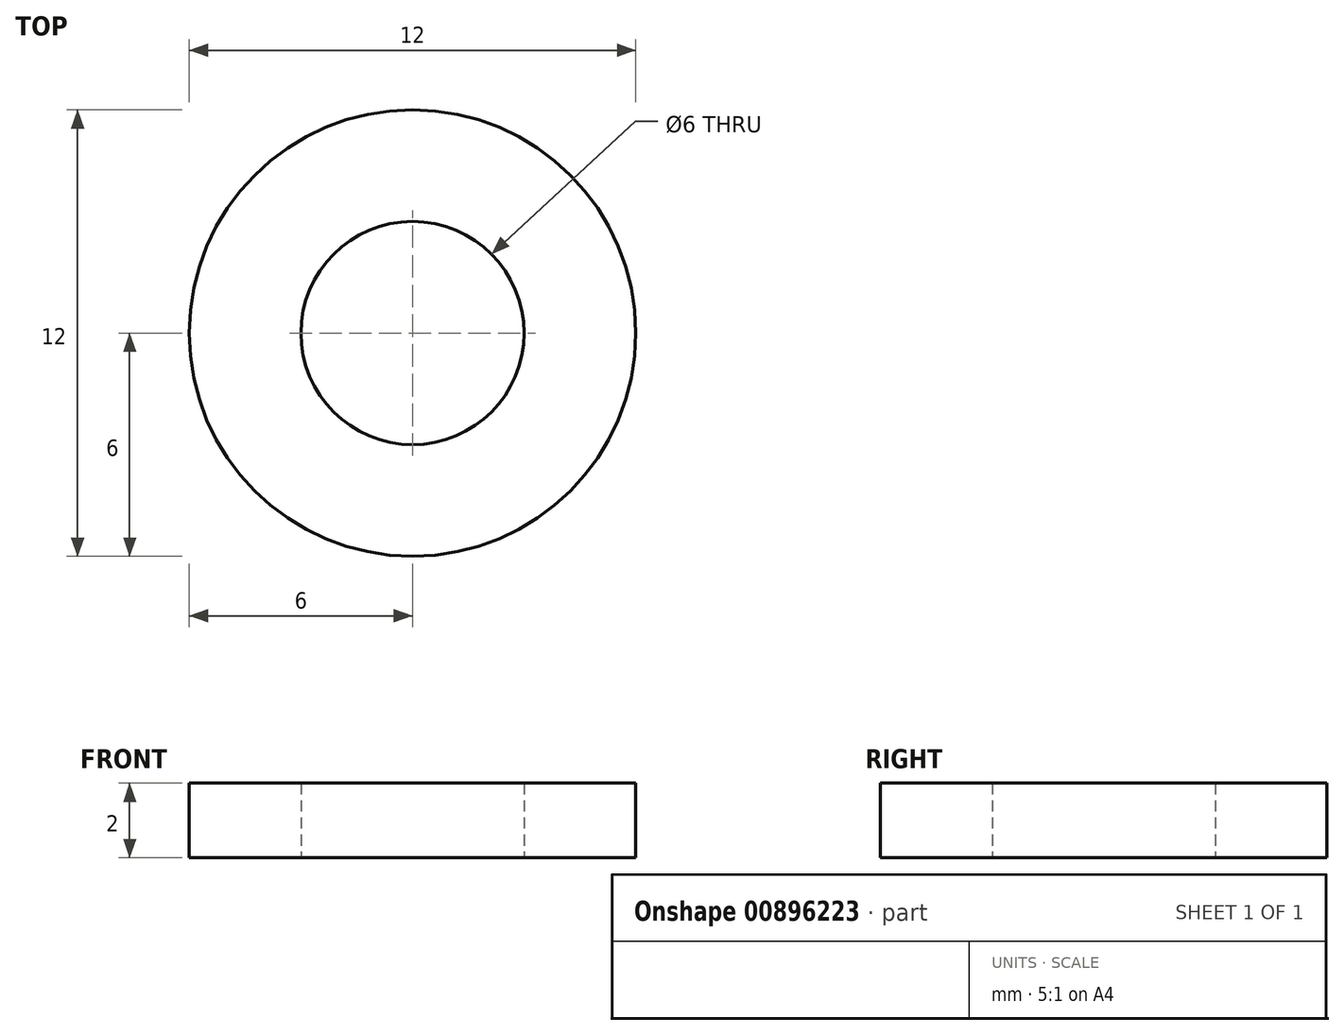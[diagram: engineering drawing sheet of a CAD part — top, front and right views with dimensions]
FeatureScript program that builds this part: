
annotation { "Feature Type Name" : "Feature", "Feature Type Description" : "" }
export const myFeature = defineFeature(function(context is Context, id is Id, definition is map)
    precondition{}
    {
        {
            var Q0;
            Q0=qCreatedBy(makeId("Top.planeOp"),FACE);
            var sketch = newSketch(context, id + "F0", { "sketchPlane" : qUnion([Q0])});
            skCircle(sketch, "E0", {"center": v(0, 0) * mm, "radius": 6 * mm});
            skPoint(sketch, "E1", {"position": v(0, 6) * mm});
            skSolve(sketch);
        }
        {
            var Q0;
            Q0 = qSketchRegion(id + "F0", true);
            extrude(context, id + "F1", {"entities" : qUnion([Q0]), "depth" : 2 * mm, "offsetDistance" : 25 * mm});
        }
        {
            var Q0;
            Q0=sQuery(id+"F0.wireOp",VERTEX,"E0.center");
            var Q1;
            Q1=makeQuery(id+"F1.opExtrude","SWEPT_BODY",BODY,{"disambiguationData":[OSD([sQuery(id+"F0.wireOp",EDGE,"E0")])]});
            hole(context, id + "F2", {"style" : HoleStyle.SIMPLE, "endStyle" : HoleEndStyle.THROUGH, "oppositeDirection" : true, "holeDiameter" : 6 * mm, "majorDiameter" : 5 * mm, "isTappedThrough" : true, "tappedDepth" : 12 * mm, "tapClearance" : 3, "locations" : qUnion([Q0]), "scope" : qUnion([Q1])});
        }
    });
